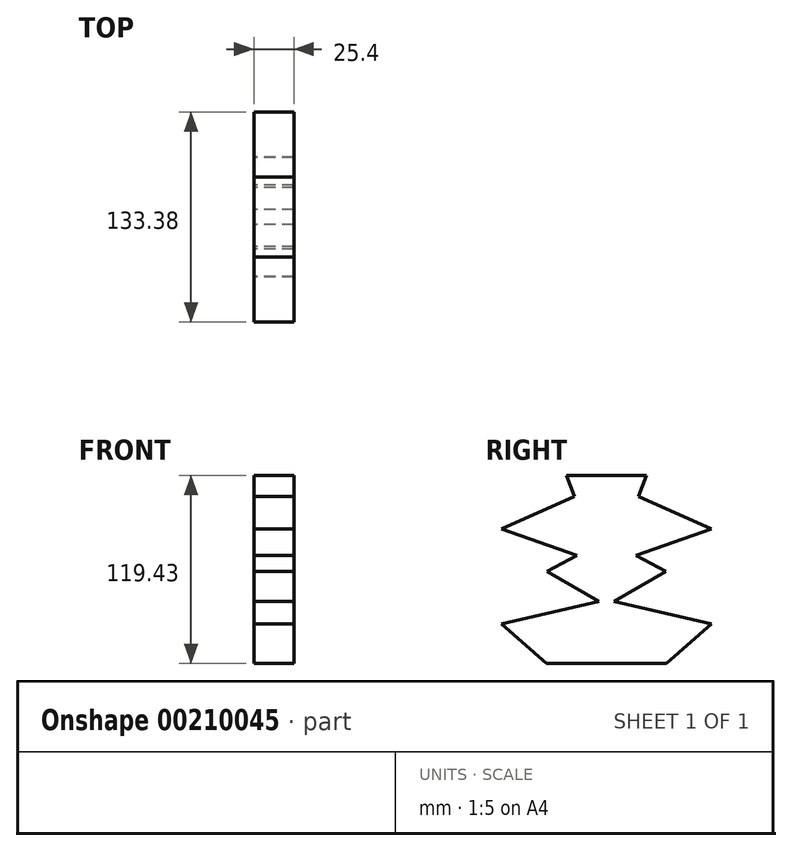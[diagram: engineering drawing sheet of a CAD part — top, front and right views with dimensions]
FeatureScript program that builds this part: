
annotation { "Feature Type Name" : "Feature", "Feature Type Description" : "" }
export const myFeature = defineFeature(function(context is Context, id is Id, definition is map)
    precondition{}
    {
        {
            var Q0;
            Q0=qCreatedBy(makeId("Right.planeOp"),FACE);
            var sketch = newSketch(context, id + "F0", { "sketchPlane" : qUnion([Q0])});
            skLineSegment(sketch, "E0", {"start": v(0, 64.38) * mm, "end": v(25.4, 64.38) * mm});
            skLineSegment(sketch, "E1", {"start": v(25.4, 64.38) * mm, "end": v(20.28, 50.95) * mm});
            skLineSegment(sketch, "E2", {"start": v(20.28, 50.95) * mm, "end": v(66.69, 30.28) * mm});
            skLineSegment(sketch, "E3", {"start": v(66.69, 30.28) * mm, "end": v(18.75, 13.47) * mm});
            skLineSegment(sketch, "E4", {"start": v(18.75, 13.47) * mm, "end": v(37.7, 3.44) * mm});
            skLineSegment(sketch, "E5", {"start": v(37.7, 3.44) * mm, "end": v(4.78, -15.73) * mm});
            skLineSegment(sketch, "E6", {"start": v(4.78, -15.73) * mm, "end": v(66.69, -29.86) * mm});
            skLineSegment(sketch, "E7", {"start": v(66.69, -29.86) * mm, "end": v(38.1, -55.05) * mm});
            skLineSegment(sketch, "E8", {"start": v(38.1, -55.05) * mm, "end": v(25.4, -55.05) * mm});
            skLineSegment(sketch, "E9", {"start": v(25.4, -55.05) * mm, "end": v(0, -55.05) * mm});
            skLineSegment(sketch, "E10.MirrorCS", {"start": v(0, 64.38) * mm, "end": v(-25.4, 64.38) * mm});
            skLineSegment(sketch, "E11.MirrorCS", {"start": v(-25.4, 64.38) * mm, "end": v(-20.28, 50.95) * mm});
            skLineSegment(sketch, "E12.MirrorCS", {"start": v(-20.28, 50.95) * mm, "end": v(-66.69, 30.28) * mm});
            skLineSegment(sketch, "E13.MirrorCS", {"start": v(-37.7, 3.44) * mm, "end": v(-4.78, -15.73) * mm});
            skLineSegment(sketch, "E14.MirrorCS", {"start": v(-18.75, 13.47) * mm, "end": v(-37.7, 3.44) * mm});
            skLineSegment(sketch, "E15.MirrorCS", {"start": v(-25.4, -55.05) * mm, "end": v(0, -55.05) * mm});
            skLineSegment(sketch, "E16.MirrorCS", {"start": v(-38.1, -55.05) * mm, "end": v(-25.4, -55.05) * mm});
            skLineSegment(sketch, "E17.MirrorCS", {"start": v(-66.69, -29.86) * mm, "end": v(-38.1, -55.05) * mm});
            skLineSegment(sketch, "E18.MirrorCS", {"start": v(-4.78, -15.73) * mm, "end": v(-66.69, -29.86) * mm});
            skLineSegment(sketch, "E19.MirrorCS", {"start": v(-66.69, 30.28) * mm, "end": v(-18.75, 13.47) * mm});
            skSolve(sketch);
        }
        {
            var Q0;
            Q0=makeQuery(id+"F0.imprint","IMPRINT",FACE,{"disambiguationData":[TD([[makeQuery(id+"F0.imprint","IMPRINT",EDGE,{"derivedFrom":sQuery(id+"F0.wireOp",EDGE,"E0")}),-1.0]])]});
            extrude(context, id + "F1", {"entities" : qUnion([Q0]), "depth" : 25.4 * mm});
        }
    });
